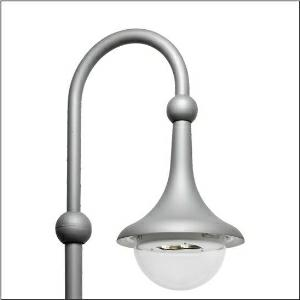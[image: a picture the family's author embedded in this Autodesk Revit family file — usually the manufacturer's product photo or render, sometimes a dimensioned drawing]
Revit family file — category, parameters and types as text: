
# Revit family: grosse_glocke_iq___st1_2a_5xa1565e1f108_d4d8
name_source: partatom
category: Lighting Fixtures
units: mm (PartAtom-declared; Revit-internal decimal feet)

## family parameters
Cut with Voids When Loaded = No
Host = Face
Light Source = No
Part Type = Normal
Room Calculation Point = No
Round Connector Dimension = Use Diameter
Shared = No

## types (1)
- --- (1 x LED, 5180 lm, 34.3 W, 3000K)
    Apparent Load = 34 VA
    CIE Flux Codes = 28 66 95 100 100
    Color Rendering = 70
    Color Temperature = 3000K
    Default Elevation = 1800 mm
    Description = Large Bell iQ, mast luminaire, primary light control with 3 zone facetted reflector, of plastic, silver coated, primary optical cover: enclosure, of PMMA, transparent, light distribution: ST1.2a, light emission: direct distribution, primary light characteristic: asymmetric, installation type: suspended mounting, High Power LED, rated luminous flux: 5.180lm, luminous efficacy: 151lm/W, light colour: 730, colour temperature: 3000K, control gear: iQ Street-Remote, control: optimised constant luminous flux control (CLO 2.0), Desk-Remote (wireless, voltage-free reading and setting of iQ features in the workshop via application-optimized NFC function/RFID function), Light-Fading, Smart-Wire, Night-Set, Lumen-Switch, Temp-Guard, Auto-Match, Street-Remote, pre-setting: logarithmic dimming characteristic, mains connection: 230..240V, AC, 50/60Hz, start of lifetime: 34W, end of service life: 38W, reduction: 16W, luminaire housing, bell-shaped, of glass-fibre reinforced polyester, coated, Siteco® metallic grey (DB 702S), please order curved mast extension separately, diameter: 530mm, height: 695mm, mounting height: 4..6m, protection rating (complete): IP54, insulation class (complete): insulation class II (safety insulation), certification: CE, ENEC, VDE, impact resistance: IK08, standard-compliant lighting for roads and squares, packaging unit: 1 piece

Light Distribution: ST1.2a
    Height = 695 mm
    Lamp = 1 x LED
    Lamp Light Flux = 5180 lm
    Lamp Power = 34.3 W
    Lamp count = 1
    Length = 530 mm
    Luminous efficacy = 151 lm/W
    Manufacturer = Siteco
    ModVariant = No
    Model = 5XA1565E1F108
    Number of Poles = 1
    OnlyDefault = Yes
    Power Factor = 1
    Product Name = Große Glocke iQ | ST1.2a
    Product group = mast luminaire | pylon annexe
    ProductGroupID = 6200
    Protection Class = Protection class II
    Protection Degree = IP 54
    RLX_Detail_Level = 1
    RLX_Emergency_Light_Flux = 0 lm
    RLX_Emergency_Type = 0
    RLX_Emergency_Type_DB = No
    RlxData = <blob elided: 71897 chars, md5=8fdb73be>
    Socket = socket
    Standby Power = 0 W
    System Light Flux = 5180 lm
    System Power = 34 W
    Type Comments = factory setting: luminous flux: 100 % | dim-lin: 254 | 640 mA
    Type Image = l_1347688.jpg
    URL = http://relux.com
    VarID = @adj_079943
    Voltage = 0 V
    Weight = 0.00 kg
    Width = 0 mm  [stored 0 ft]

note: [stored X ft] marks values corroborated as IEEE doubles in the binary element streams (Revit-internal decimal feet)

## geometry (parser evidence)
native form markers: Blend x4, Sweep x10
no freeform markers — native parametric forms only
